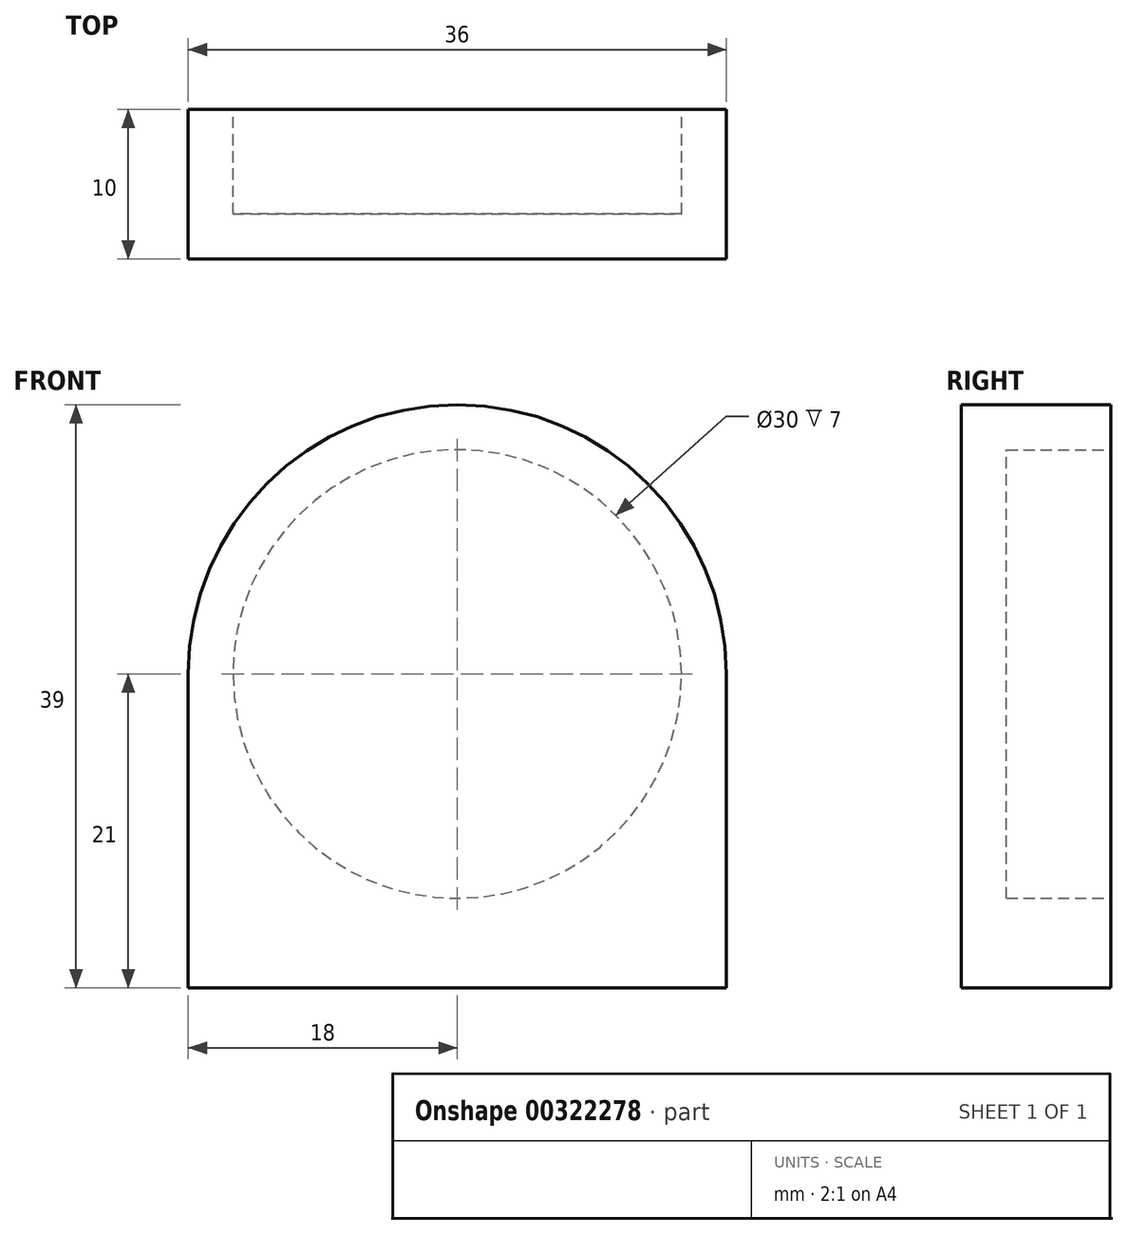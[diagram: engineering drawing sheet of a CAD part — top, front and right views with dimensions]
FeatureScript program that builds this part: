
annotation { "Feature Type Name" : "Feature", "Feature Type Description" : "" }
export const myFeature = defineFeature(function(context is Context, id is Id, definition is map)
    precondition{}
    {
        {
            var Q0;
            Q0=qCreatedBy(makeId("Front.planeOp"),FACE);
            var sketch = newSketch(context, id + "F0", { "sketchPlane" : qUnion([Q0])});
            skLineSegment(sketch, "E0.bottom", {"start": v(-18, 1.5) * mm, "end": v(18, 1.5) * mm});
            skLineSegment(sketch, "E0.top", {"start": v(-18, -1.5) * mm, "end": v(18, -1.5) * mm});
            skLineSegment(sketch, "E0.left", {"start": v(-18, 1.5) * mm, "end": v(-18, -1.5) * mm});
            skLineSegment(sketch, "E0.right", {"start": v(18, 1.5) * mm, "end": v(18, -1.5) * mm});
            skPoint(sketch, "E0.middle", {"position": v(0, 0) * mm});
            skCircle(sketch, "E1", {"center": v(0, 19.5) * mm, "radius": 18 * mm});
            skCircle(sketch, "E2", {"center": v(0, 19.5) * mm, "radius": 15 * mm});
            skLineSegment(sketch, "E3", {"start": v(0, 19.5) * mm, "end": v(15, 19.5) * mm});
            skLineSegment(sketch, "E4", {"start": v(0, 34.5) * mm, "end": v(0, 37.5) * mm});
            skLineSegment(sketch, "E5", {"start": v(0, 19.5) * mm, "end": v(-15, 19.5) * mm});
            skLineSegment(sketch, "E6", {"start": v(-15, 19.5) * mm, "end": v(-18, 19.5) * mm});
            skLineSegment(sketch, "E7", {"start": v(15, 19.5) * mm, "end": v(18, 19.5) * mm});
            skLineSegment(sketch, "E8", {"start": v(-18, 19.5) * mm, "end": v(-18, 1.5) * mm});
            skLineSegment(sketch, "E9", {"start": v(18, 1.5) * mm, "end": v(18, 19.5) * mm});
            skLineSegment(sketch, "E10", {"start": v(0, 1.5) * mm, "end": v(0, 1.5) * mm});
            skSolve(sketch);
        }
        {
            var Q0;
            {var subQ0=sQuery(id+"F0.wireOp",EDGE,"E3");Q0=makeQuery(id+"F0.imprint","IMPRINT",FACE,{"disambiguationData":[TD([[makeQuery(id+"F0.imprint","IMPRINT",EDGE,{"derivedFrom":subQ0}),1.0]])]});}
            var Q1;
            {var subQ0=sQuery(id+"F0.wireOp",EDGE,"E6");Q1=makeQuery(id+"F0.imprint","IMPRINT",FACE,{"disambiguationData":[TD([[makeQuery(id+"F0.imprint","IMPRINT",EDGE,{"derivedFrom":subQ0}),1.0]])]});}
            var Q2;
            Q2=makeQuery(id+"F0.imprint","IMPRINT",FACE,{"disambiguationData":[TD([[makeQuery(id+"F0.imprint","IMPRINT",EDGE,{"derivedFrom":sQuery(id+"F0.wireOp",EDGE,"E0.top")}),1.0]])]});
            var Q3;
            {var subQ0=sQuery(id+"F0.wireOp",EDGE,"E9");Q3=makeQuery(id+"F0.imprint","IMPRINT",FACE,{"disambiguationData":[TD([[makeQuery(id+"F0.imprint","IMPRINT",EDGE,{"derivedFrom":subQ0}),1.0]])]});}
            var Q4;
            {var subQ0=sQuery(id+"F0.wireOp",EDGE,"E3");Q4=makeQuery(id+"F0.imprint","IMPRINT",FACE,{"disambiguationData":[TD([[makeQuery(id+"F0.imprint","IMPRINT",EDGE,{"derivedFrom":subQ0}),-1.0]])]});}
            var Q5;
            {var subQ0=sQuery(id+"F0.wireOp",EDGE,"E4");Q5=makeQuery(id+"F0.imprint","IMPRINT",FACE,{"disambiguationData":[TD([[makeQuery(id+"F0.imprint","IMPRINT",EDGE,{"derivedFrom":subQ0}),-1.0]])]});}
            var Q6;
            {var subQ0=sQuery(id+"F0.wireOp",EDGE,"E4");Q6=makeQuery(id+"F0.imprint","IMPRINT",FACE,{"disambiguationData":[TD([[makeQuery(id+"F0.imprint","IMPRINT",EDGE,{"derivedFrom":subQ0}),1.0]])]});}
            var Q7;
            {var subQ0=sQuery(id+"F0.wireOp",EDGE,"E8");Q7=makeQuery(id+"F0.imprint","IMPRINT",FACE,{"disambiguationData":[TD([[makeQuery(id+"F0.imprint","IMPRINT",EDGE,{"derivedFrom":subQ0}),1.0]])]});}
            extrude(context, id + "F1", {"entities" : qUnion([Q0, Q1, Q2, Q3, Q4, Q5, Q6, Q7]), "depth" : 10 * mm});
        }
        {
            var Q0;
            {var subQ0=sQuery(id+"F0.wireOp",EDGE,"E3");Q0=makeQuery(id+"F0.imprint","IMPRINT",FACE,{"disambiguationData":[TD([[makeQuery(id+"F0.imprint","IMPRINT",EDGE,{"derivedFrom":subQ0}),-1.0]])]});}
            var Q1;
            {var subQ0=sQuery(id+"F0.wireOp",EDGE,"E3");Q1=makeQuery(id+"F0.imprint","IMPRINT",FACE,{"disambiguationData":[TD([[makeQuery(id+"F0.imprint","IMPRINT",EDGE,{"derivedFrom":subQ0}),1.0]])]});}
            extrude(context, id + "F2", {"entities" : qUnion([Q0, Q1]), "operationType" : NewBodyOperationType.REMOVE, "depth" : 7 * mm});
        }
    });
